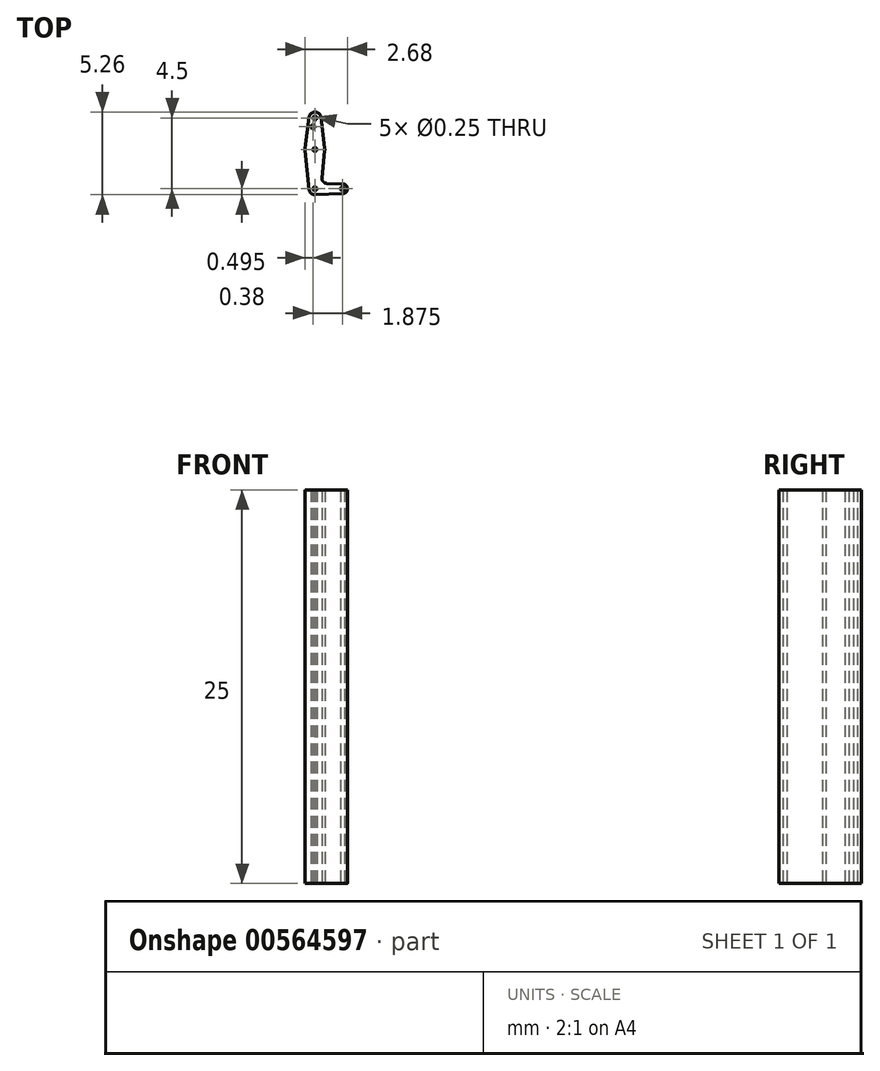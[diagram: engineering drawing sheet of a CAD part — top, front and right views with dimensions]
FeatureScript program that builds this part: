
annotation { "Feature Type Name" : "Feature", "Feature Type Description" : "" }
export const myFeature = defineFeature(function(context is Context, id is Id, definition is map)
    precondition{}
    {
        {
            var Q0;
            Q0=qCreatedBy(makeId("Top.planeOp"),FACE);
            var sketch = newSketch(context, id + "F0", { "sketchPlane" : qUnion([Q0])});
            skCircle(sketch, "E0", {"center": v(0, 0) * mm, "radius": 0.38 * mm});
            skCircle(sketch, "E1", {"center": v(1.75, 0) * mm, "radius": 0.31 * mm});
            skCircle(sketch, "E2", {"center": v(0, 4.5) * mm, "radius": 0.38 * mm});
            skPoint(sketch, "E3.center.orphan", {"position": v(0, 2.25) * mm});
            skCircle(sketch, "E4", {"center": v(0, 2.5) * mm, "radius": 0.62 * mm});
            skLineSegment(sketch, "E5", {"start": v(-0.37, 4.55) * mm, "end": v(-0.62, 2.58) * mm});
            skLineSegment(sketch, "E6", {"start": v(0.37, 4.55) * mm, "end": v(0.62, 2.58) * mm});
            skLineSegment(sketch, "E7", {"start": v(-0.37, -0.04) * mm, "end": v(-0.62, 2.44) * mm});
            skLineSegment(sketch, "E8", {"start": v(0.45, 0.7) * mm, "end": v(0.62, 2.44) * mm});
            skLineSegment(sketch, "E9", {"start": v(0.75, 0.35) * mm, "end": v(1.76, 0.31) * mm});
            skLineSegment(sketch, "E10", {"start": v(0.01, -0.37) * mm, "end": v(1.76, -0.31) * mm});
            skCircle(sketch, "E11", {"center": v(0, 4.5) * mm, "radius": 0.12 * mm});
            skCircle(sketch, "E12", {"center": v(0, 2.5) * mm, "radius": 0.12 * mm});
            skCircle(sketch, "E13", {"center": v(0, 0) * mm, "radius": 0.12 * mm});
            skCircle(sketch, "E14", {"center": v(1.75, 0) * mm, "radius": 0.12 * mm});
            skCircle(sketch, "E15", {"center": v(-0.12, 3.94) * mm, "radius": 0.12 * mm});
            skArc(sketch, "E16.filletArc", {"start": v(0.45, 0.7) * mm, "mid": v(0.52, 0.46) * mm, "end": v(0.75, 0.35) * mm});
            skSolve(sketch);
        }
        {
            var Q0;
            Q0 = qSketchRegion(id + "F0", true);
            extrude(context, id + "F1", {"entities" : qUnion([Q0]), "depth" : 25 * mm, "offsetDistance" : 25 * mm});
        }
        {
            var Q0;
            Q0 = qSketchRegion(id + "F0", true);
            extrude(context, id + "F2", {"entities" : qUnion([Q0]), "operationType" : NewBodyOperationType.ADD, "depth" : 3.05 * mm, "offsetDistance" : 25 * mm});
        }
    });
